# Revit family: Range-Hood
name_source: partatom
category: Mechanical Equipment
units: mm (PartAtom-declared; Revit-internal decimal feet)

## family parameters
Always vertical = Yes
Classification Number = 23.40.40.14.21
Cut with Voids When Loaded = No
Host = Ceiling
Maintain Annotation Orientation = No
Part Type = Normal
Room Calculation Point = No
Round Connector Dimension = Use Diameter
Shared = No

## types (1)
- Range-Hood
    Amperage = 3.4
    Assembly Code = D3040200
    Body Material = ARCAT - Metal - Steel, Stainless
    CFM = 300
    Construction Details = http://www.arcat.com
    Default Elevation = 0' - 0"
    Depth = 1' - 8"
    Description = Residential Range Hood
    Duct Size = 0' - 8"
    Expected Lifespan (Years) = 15
    Green Building-LEED = http://www.arcat.com
    Height = 5' - 8"
    Keynote = 11450
    Maintenance Schedule (Months) = 6
    Manufacturer = Generic
    Manufacturer Fax = (203) 929-2444
    Manufacturer Website = http://www.arcat.com
    Model = Generic
    Motor RPM = 1550
    Product Data = http://www.arcat.com
    Product Properties = http://www.arcat.com
    Specification = http://www.arcat.com
    URL = http://www.arcat.com
    Voltage = 115
    Warranty Duration (Years) = 2
    Wattage = 391
    Width = 3' - 0"

## geometry (parser evidence)
native form markers: Sweep x4
no freeform markers — native parametric forms only
